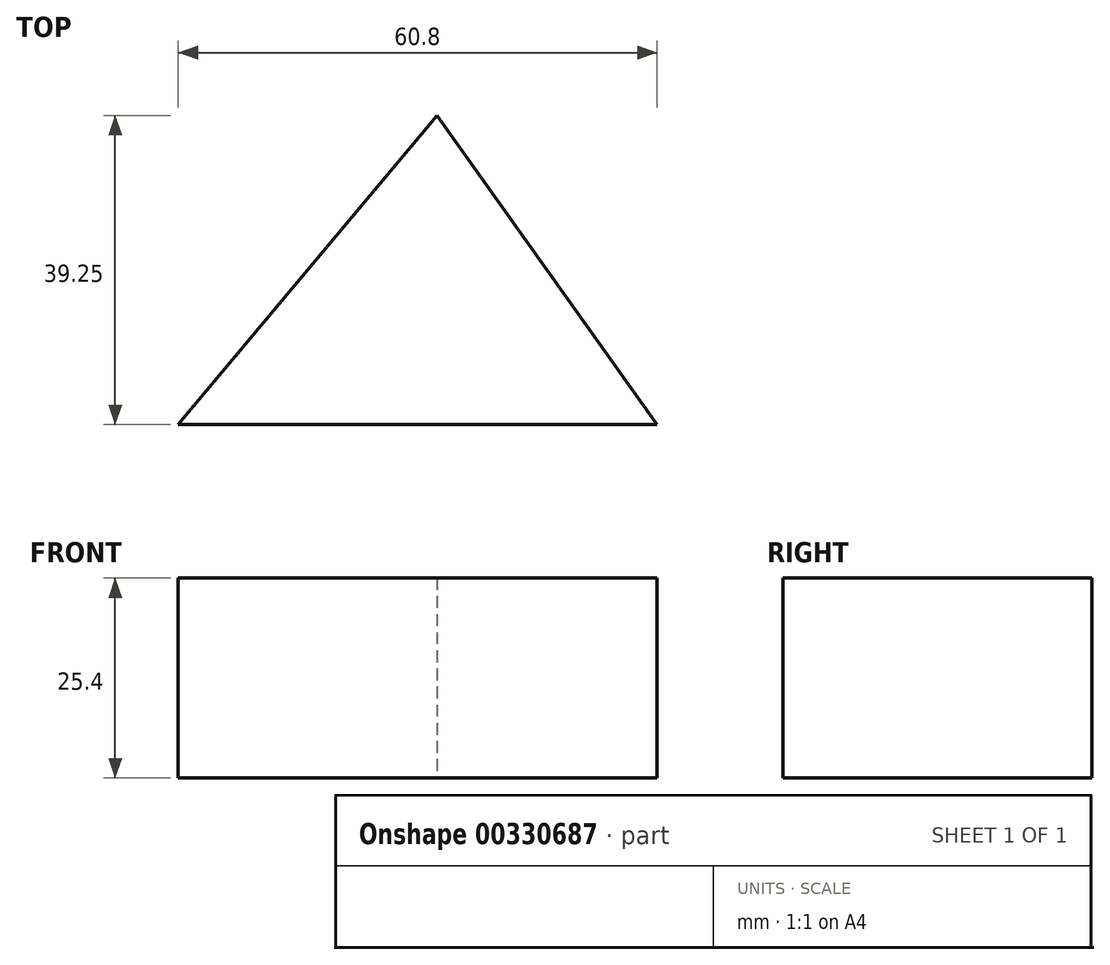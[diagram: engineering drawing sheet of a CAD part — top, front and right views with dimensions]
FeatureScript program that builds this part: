
annotation { "Feature Type Name" : "Feature", "Feature Type Description" : "" }
export const myFeature = defineFeature(function(context is Context, id is Id, definition is map)
    precondition{}
    {
        {
            var Q0;
            Q0=qCreatedBy(makeId("Top.planeOp"),FACE);
            var sketch = newSketch(context, id + "F0", { "sketchPlane" : qUnion([Q0])});
            skLineSegment(sketch, "E0", {"start": v(-27.4, -10.65) * mm, "end": v(5.44, 28.6) * mm});
            skLineSegment(sketch, "E1", {"start": v(5.44, 28.6) * mm, "end": v(33.4, -10.65) * mm});
            skLineSegment(sketch, "E2", {"start": v(-27.4, -10.65) * mm, "end": v(33.4, -10.65) * mm});
            skSolve(sketch);
        }
        {
            var Q0;
            Q0 = qSketchRegion(id + "F0", true);
            extrude(context, id + "F1", {"entities" : qUnion([Q0]), "depth" : 25.4 * mm});
        }
    });
